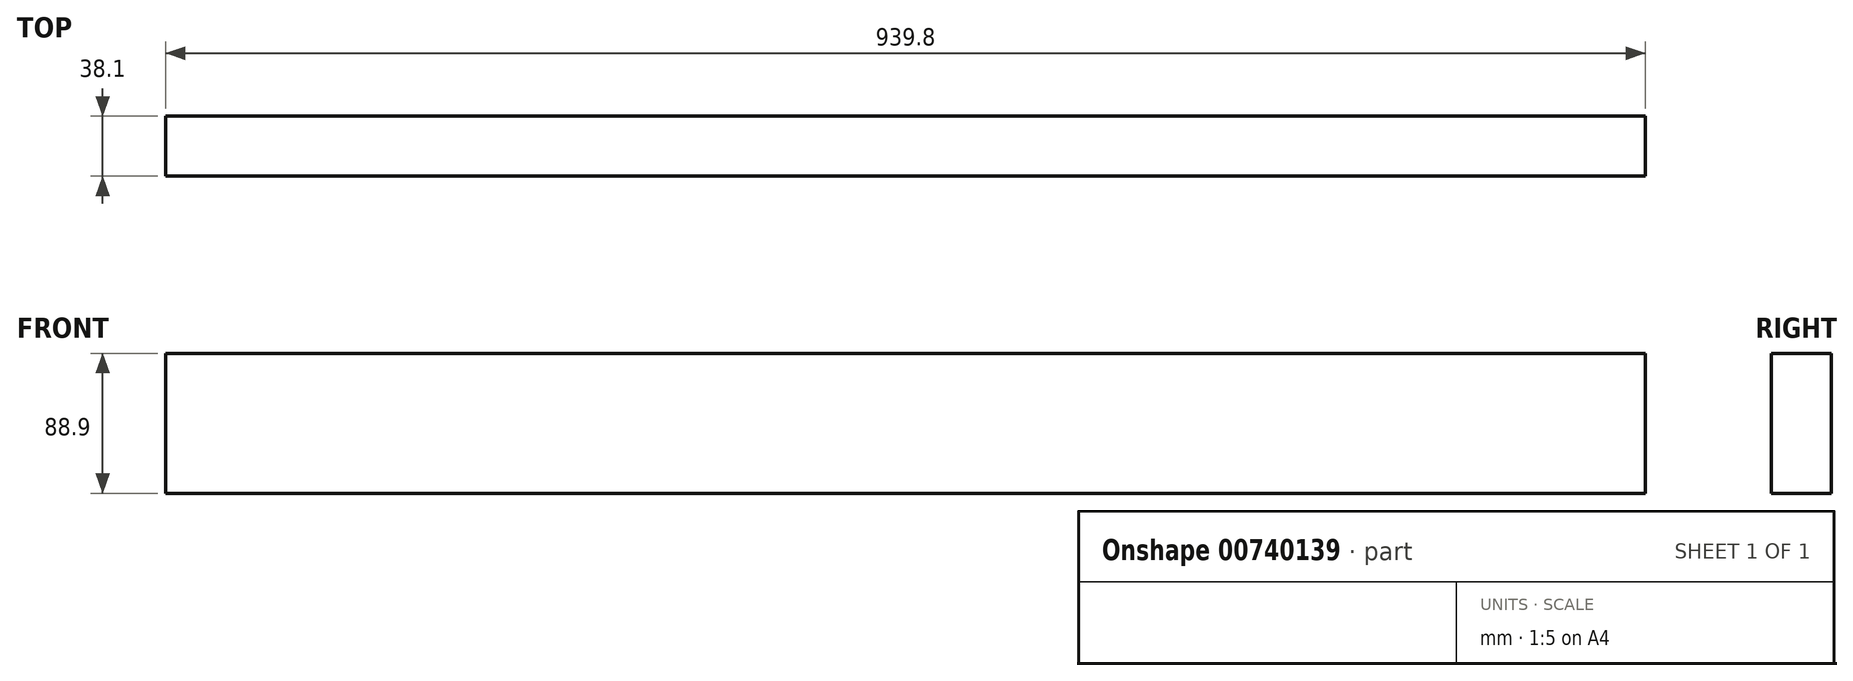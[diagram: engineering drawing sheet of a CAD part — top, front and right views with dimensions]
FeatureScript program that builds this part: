
annotation { "Feature Type Name" : "Feature", "Feature Type Description" : "" }
export const myFeature = defineFeature(function(context is Context, id is Id, definition is map)
    precondition{}
    {
        {
            var Q0;
            Q0=qCreatedBy(makeId("Right.planeOp"),FACE);
            var sketch = newSketch(context, id + "F0", { "sketchPlane" : qUnion([Q0])});
            skLineSegment(sketch, "E0.bottom", {"start": v(-79.68, 85.36) * mm, "end": v(-41.58, 85.36) * mm});
            skLineSegment(sketch, "E0.top", {"start": v(-79.68, -3.54) * mm, "end": v(-41.58, -3.54) * mm});
            skLineSegment(sketch, "E0.left", {"start": v(-79.68, 85.36) * mm, "end": v(-79.68, -3.54) * mm});
            skLineSegment(sketch, "E0.right", {"start": v(-41.58, 85.36) * mm, "end": v(-41.58, -3.54) * mm});
            skSolve(sketch);
        }
        {
            var Q0;
            Q0=makeQuery(id+"F0.imprint","IMPRINT",FACE,{"disambiguationData":[TD([[makeQuery(id+"F0.imprint","IMPRINT",EDGE,{"derivedFrom":sQuery(id+"F0.wireOp",EDGE,"E0.bottom")}),-1.0]])]});
            extrude(context, id + "F1", {"entities" : qUnion([Q0]), "depth" : 939.8 * mm, "offsetDistance" : 25.4 * mm});
        }
    });
